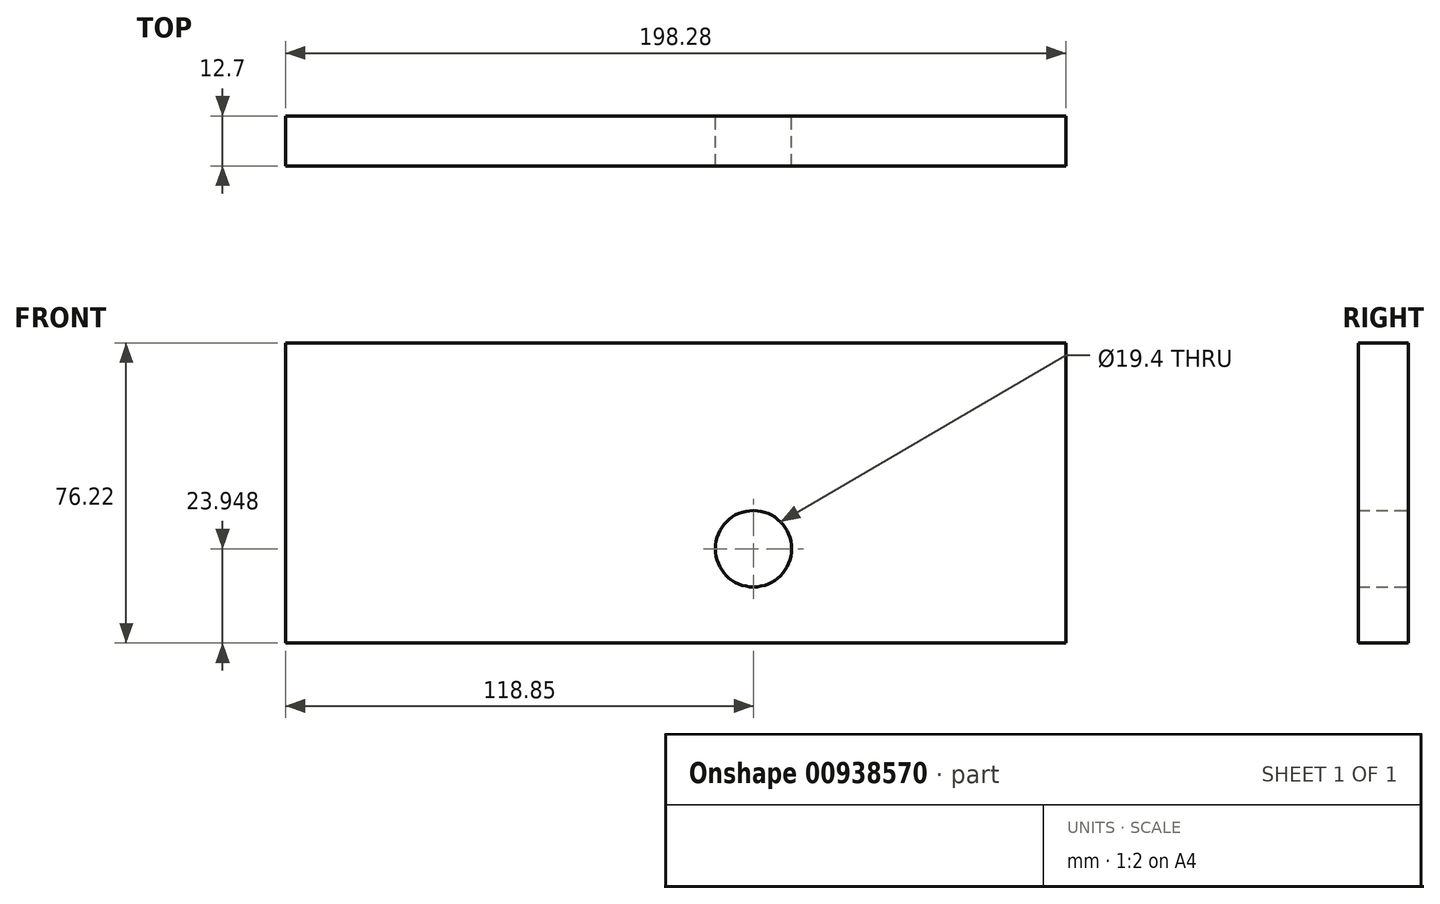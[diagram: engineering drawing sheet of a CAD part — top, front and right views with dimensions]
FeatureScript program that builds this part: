
annotation { "Feature Type Name" : "Feature", "Feature Type Description" : "" }
export const myFeature = defineFeature(function(context is Context, id is Id, definition is map)
    precondition{}
    {
        {
            var Q0;
            Q0=qCreatedBy(makeId("Front.planeOp"),FACE);
            var sketch = newSketch(context, id + "F0", { "sketchPlane" : qUnion([Q0])});
            skLineSegment(sketch, "E0.bottom", {"start": v(-99.14, 38.1) * mm, "end": v(99.14, 38.1) * mm});
            skLineSegment(sketch, "E0.top", {"start": v(-99.14, -38.1) * mm, "end": v(99.14, -38.1) * mm});
            skLineSegment(sketch, "E0.left", {"start": v(-99.14, 38.1) * mm, "end": v(-99.14, -38.1) * mm});
            skLineSegment(sketch, "E0.right", {"start": v(99.14, 38.1) * mm, "end": v(99.14, -38.1) * mm});
            skPoint(sketch, "E0.middle", {"position": v(0, 0) * mm});
            skSolve(sketch);
        }
        {
            var Q0;
            Q0=makeQuery(id+"F0.imprint","IMPRINT",FACE,{"disambiguationData":[TD([[makeQuery(id+"F0.imprint","IMPRINT",EDGE,{"derivedFrom":sQuery(id+"F0.wireOp",EDGE,"E0.bottom")}),-1.0]])]});
            var sketch = newSketch(context, id + "F1", { "sketchPlane" : qUnion([Q0])});
            skCircle(sketch, "E1", {"center": v(-56.8, -14.75) * mm, "radius": 8.45 * mm});
            skSolve(sketch);
        }
        {
            var Q0;
            Q0=makeQuery(id+"F0.imprint","IMPRINT",FACE,{"disambiguationData":[TD([[makeQuery(id+"F0.imprint","IMPRINT",EDGE,{"derivedFrom":sQuery(id+"F0.wireOp",EDGE,"E0.bottom")}),-1.0]])]});
            var sketch = newSketch(context, id + "F2", { "sketchPlane" : qUnion([Q0])});
            skCircle(sketch, "E2", {"center": v(-33.73, -13.29) * mm, "radius": 8.85 * mm});
            skSolve(sketch);
        }
        {
            var Q0;
            Q0=makeQuery(id+"F0.imprint","IMPRINT",FACE,{"disambiguationData":[TD([[makeQuery(id+"F0.imprint","IMPRINT",EDGE,{"derivedFrom":sQuery(id+"F0.wireOp",EDGE,"E0.bottom")}),-1.0]])]});
            var sketch = newSketch(context, id + "F3", { "sketchPlane" : qUnion([Q0])});
            skCircle(sketch, "E3", {"center": v(19.71, -14.16) * mm, "radius": 9.7 * mm});
            skSolve(sketch);
        }
        {
            var Q0;
            Q0=makeQuery(id+"F3.imprint","IMPRINT",FACE,{"disambiguationData":[TD([[makeQuery(id+"F3.imprint","IMPRINT",EDGE,{"derivedFrom":sQuery(id+"F3.wireOp",EDGE,"E3")}),-1.0]])]});
            extrude(context, id + "F4", {"entities" : qUnion([Q0]), "depth" : 12.7 * mm, "offsetDistance" : 25.4 * mm});
        }
    });
